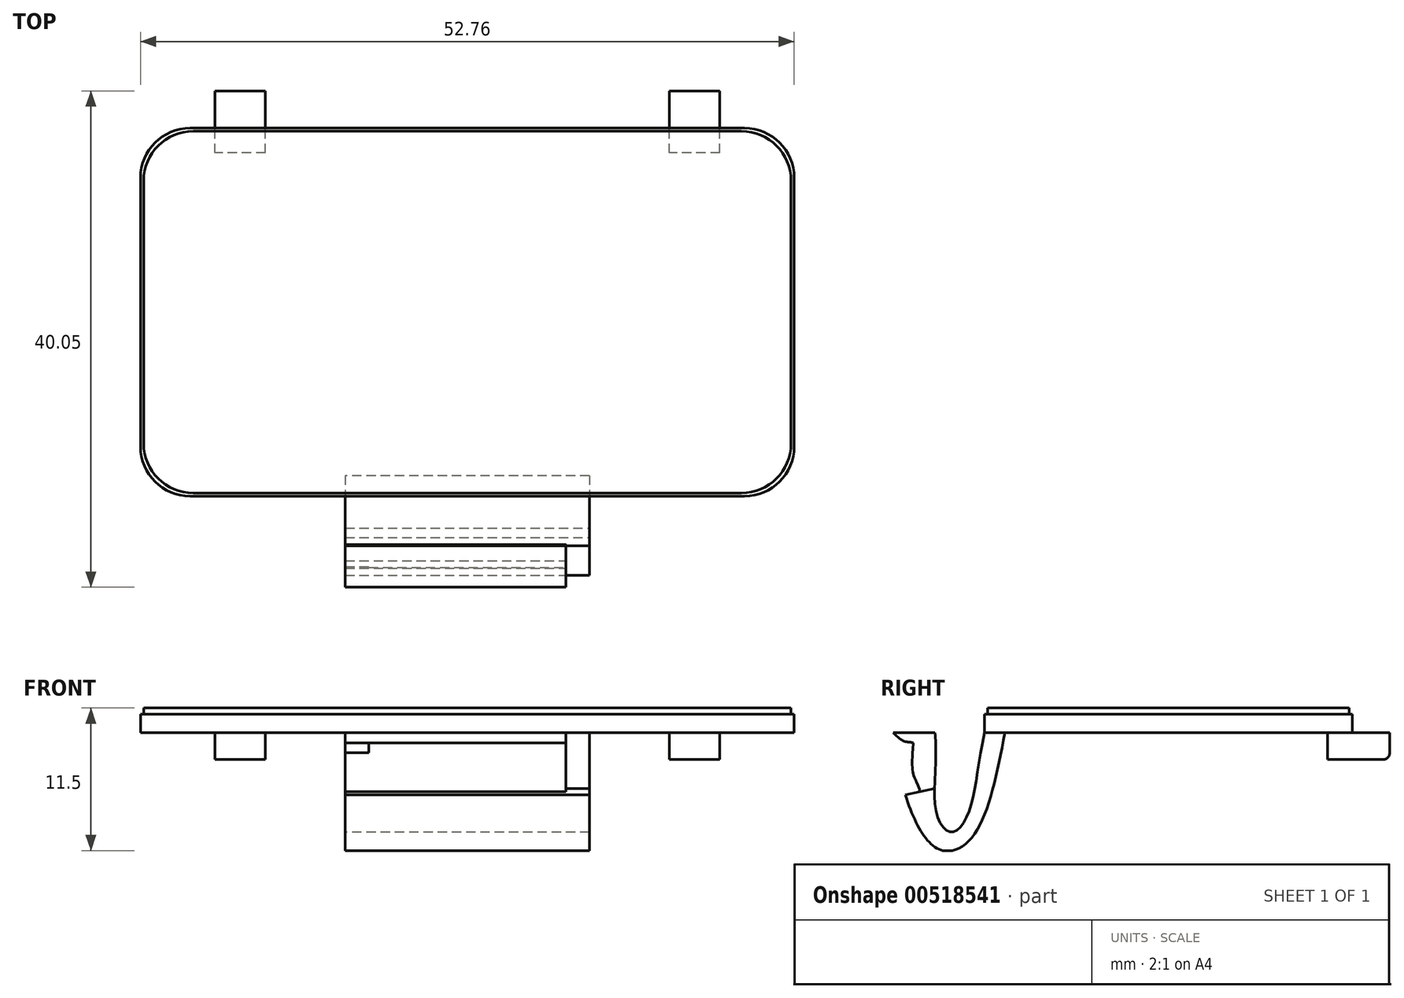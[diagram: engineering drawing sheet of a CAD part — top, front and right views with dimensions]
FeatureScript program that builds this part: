
annotation { "Feature Type Name" : "Feature", "Feature Type Description" : "" }
export const myFeature = defineFeature(function(context is Context, id is Id, definition is map)
    precondition{}
    {
        {
            var Q0;
            Q0=qCreatedBy(makeId("Top.planeOp"),FACE);
            var sketch = newSketch(context, id + "F0", { "sketchPlane" : qUnion([Q0])});
            skLineSegment(sketch, "E0.bottom", {"start": v(22.38, 14.85) * mm, "end": v(-22.38, 14.85) * mm});
            skLineSegment(sketch, "E0.top", {"start": v(22.38, -14.85) * mm, "end": v(-22.38, -14.85) * mm});
            skLineSegment(sketch, "E0.left", {"start": v(26.38, 10.85) * mm, "end": v(26.38, -10.85) * mm});
            skLineSegment(sketch, "E0.right", {"start": v(-26.38, 10.85) * mm, "end": v(-26.38, -10.85) * mm});
            skPoint(sketch, "E0.middle", {"position": v(0, 0) * mm});
            skPoint(sketch, "E1.visualSharp", {"position": v(26.38, 14.85) * mm});
            skArc(sketch, "E1.filletArc", {"start": v(26.38, 10.85) * mm, "mid": v(25.2, 13.68) * mm, "end": v(22.38, 14.85) * mm});
            skPoint(sketch, "E2.visualSharp", {"position": v(26.38, -14.85) * mm});
            skArc(sketch, "E2.filletArc", {"start": v(22.38, -14.85) * mm, "mid": v(25.2, -13.68) * mm, "end": v(26.38, -10.85) * mm});
            skPoint(sketch, "E3.visualSharp", {"position": v(-26.38, -14.85) * mm});
            skArc(sketch, "E3.filletArc", {"start": v(-26.38, -10.85) * mm, "mid": v(-25.2, -13.68) * mm, "end": v(-22.38, -14.85) * mm});
            skPoint(sketch, "E4.visualSharp", {"position": v(-26.38, 14.85) * mm});
            skArc(sketch, "E4.filletArc", {"start": v(-22.38, 14.85) * mm, "mid": v(-25.2, 13.68) * mm, "end": v(-26.38, 10.85) * mm});
            skSolve(sketch);
        }
        {
            var Q0;
            Q0=makeQuery(id+"F0.imprint","IMPRINT",FACE,{"disambiguationData":[TD([[makeQuery(id+"F0.imprint","IMPRINT",EDGE,{"derivedFrom":sQuery(id+"F0.wireOp",EDGE,"E0.bottom")}),1.0]])]});
            extrude(context, id + "F1", {"entities" : qUnion([Q0]), "depth" : 1.5 * mm, "offsetDistance" : 25.4 * mm});
        }
        {
            var Q0;
            Q0=makeQuery(id+"F1.opExtrude","CAP_FACE",FACE,{"disambiguationData":[OSD([sQuery(id+"F0.wireOp",EDGE,"E0.bottom"),sQuery(id+"F0.wireOp",EDGE,"E0.top"),sQuery(id+"F0.wireOp",EDGE,"E0.left"),sQuery(id+"F0.wireOp",EDGE,"E0.right"),sQuery(id+"F0.wireOp",EDGE,"E1.filletArc"),sQuery(id+"F0.wireOp",EDGE,"E2.filletArc"),sQuery(id+"F0.wireOp",EDGE,"E3.filletArc"),sQuery(id+"F0.wireOp",EDGE,"E4.filletArc")])],"isStart":false});
            var sketch = newSketch(context, id + "F2", { "sketchPlane" : qUnion([Q0])});
            skLineSegment(sketch, "E5.bottom", {"start": v(22.12, 14.6) * mm, "end": v(-22.13, 14.6) * mm});
            skLineSegment(sketch, "E5.top", {"start": v(22.12, -14.6) * mm, "end": v(-22.13, -14.6) * mm});
            skLineSegment(sketch, "E5.left", {"start": v(26.13, 10.6) * mm, "end": v(26.13, -10.6) * mm});
            skLineSegment(sketch, "E5.right", {"start": v(-26.13, 10.6) * mm, "end": v(-26.13, -10.6) * mm});
            skPoint(sketch, "E5.middle", {"position": v(0, 0) * mm});
            skPoint(sketch, "E6.visualSharp", {"position": v(-26.13, 14.6) * mm});
            skArc(sketch, "E6.filletArc", {"start": v(-22.13, 14.6) * mm, "mid": v(-24.95, 13.43) * mm, "end": v(-26.13, 10.6) * mm});
            skPoint(sketch, "E7.visualSharp", {"position": v(26.13, 14.6) * mm});
            skArc(sketch, "E7.filletArc", {"start": v(26.12, 10.6) * mm, "mid": v(24.95, 13.43) * mm, "end": v(22.12, 14.6) * mm});
            skPoint(sketch, "E8.visualSharp", {"position": v(26.13, -14.6) * mm});
            skArc(sketch, "E8.filletArc", {"start": v(22.12, -14.6) * mm, "mid": v(24.95, -13.43) * mm, "end": v(26.12, -10.6) * mm});
            skPoint(sketch, "E9.visualSharp", {"position": v(-26.13, -14.6) * mm});
            skArc(sketch, "E9.filletArc", {"start": v(-26.13, -10.6) * mm, "mid": v(-24.95, -13.43) * mm, "end": v(-22.13, -14.6) * mm});
            skSolve(sketch);
        }
        {
            var Q0;
            Q0=makeQuery(id+"F2.imprint","IMPRINT",FACE,{"disambiguationData":[TD([[makeQuery(id+"F2.imprint","IMPRINT",EDGE,{"derivedFrom":sQuery(id+"F2.wireOp",EDGE,"E5.bottom")}),1.0]])]});
            extrude(context, id + "F3", {"entities" : qUnion([Q0]), "operationType" : NewBodyOperationType.ADD, "depth" : 0.5 * mm, "offsetDistance" : 25.4 * mm});
        }
        {
            var Q0;
            Q0=makeQuery(id+"F0.imprint","IMPRINT",FACE,{"disambiguationData":[TD([[makeQuery(id+"F0.imprint","IMPRINT",EDGE,{"derivedFrom":sQuery(id+"F0.wireOp",EDGE,"E0.bottom")}),1.0]])]});
            var sketch = newSketch(context, id + "F4", { "sketchPlane" : qUnion([Q0])});
            skLineSegment(sketch, "E10.0", {"start": v(22.38, 14.85) * mm, "end": v(-22.38, 14.85) * mm, "construction": true});
            skLineSegment(sketch, "E10.1", {"start": v(22.38, -14.85) * mm, "end": v(-22.38, -14.85) * mm});
            skArc(sketch, "E10.2", {"start": v(22.38, -14.85) * mm, "mid": v(25.2, -13.68) * mm, "end": v(26.38, -10.85) * mm});
            skLineSegment(sketch, "E10.3", {"start": v(26.38, 10.85) * mm, "end": v(26.38, -10.85) * mm});
            skArc(sketch, "E10.4", {"start": v(26.38, 10.85) * mm, "mid": v(25.2, 13.68) * mm, "end": v(22.38, 14.85) * mm, "construction": true});
            skArc(sketch, "E10.5", {"start": v(-22.38, 14.85) * mm, "mid": v(-25.2, 13.68) * mm, "end": v(-26.38, 10.85) * mm, "construction": true});
            skLineSegment(sketch, "E10.6", {"start": v(-26.38, 10.85) * mm, "end": v(-26.38, -10.85) * mm});
            skArc(sketch, "E10.7", {"start": v(-26.38, -10.85) * mm, "mid": v(-25.2, -13.68) * mm, "end": v(-22.38, -14.85) * mm});
            skLineSegment(sketch, "E11", {"start": v(22.38, 14.85) * mm, "end": v(22.38, -14.85) * mm, "construction": true});
            skLineSegment(sketch, "E12", {"start": v(-22.38, 14.85) * mm, "end": v(-22.38, -14.85) * mm, "construction": true});
            skLineSegment(sketch, "E13.bottom", {"start": v(20.37, 12.85) * mm, "end": v(16.3, 12.85) * mm});
            skLineSegment(sketch, "E13.top", {"start": v(20.37, 17.85) * mm, "end": v(16.3, 17.85) * mm});
            skLineSegment(sketch, "E13.left", {"start": v(20.37, 12.85) * mm, "end": v(20.37, 17.85) * mm});
            skLineSegment(sketch, "E13.right", {"start": v(16.3, 12.85) * mm, "end": v(16.3, 17.85) * mm});
            skLineSegment(sketch, "E14.bottom", {"start": v(-16.3, 12.85) * mm, "end": v(-20.37, 12.85) * mm});
            skLineSegment(sketch, "E14.top", {"start": v(-16.3, 17.85) * mm, "end": v(-20.37, 17.85) * mm});
            skLineSegment(sketch, "E14.left", {"start": v(-16.3, 12.85) * mm, "end": v(-16.3, 17.85) * mm});
            skLineSegment(sketch, "E14.right", {"start": v(-20.37, 12.85) * mm, "end": v(-20.37, 17.85) * mm});
            skPoint(sketch, "E15", {"position": v(22.37, 12.85) * mm});
            skLineSegment(sketch, "E16", {"start": v(22.37, 12.85) * mm, "end": v(-25.84, 12.85) * mm, "construction": true});
            skLineSegment(sketch, "E17.bottom", {"start": v(9.86, -13.2) * mm, "end": v(-9.85, -13.2) * mm});
            skLineSegment(sketch, "E17.top", {"start": v(9.86, -23.2) * mm, "end": v(-9.85, -23.2) * mm});
            skLineSegment(sketch, "E17.left", {"start": v(9.86, -13.2) * mm, "end": v(9.86, -23.2) * mm});
            skLineSegment(sketch, "E17.right", {"start": v(-9.85, -13.2) * mm, "end": v(-9.85, -23.2) * mm});
            skLineSegment(sketch, "E18", {"start": v(22.38, -13.2) * mm, "end": v(-22.38, -13.2) * mm, "construction": true});
            skSolve(sketch);
        }
        {
            var Q0;
            {var subQ0=sQuery(id+"F4.wireOp",EDGE,"E14.top");Q0=makeQuery(id+"F4.imprint","IMPRINT",FACE,{"disambiguationData":[TD([[makeQuery(id+"F4.imprint","IMPRINT",EDGE,{"derivedFrom":subQ0}),1.0]])]});}
            var Q1;
            {var subQ0=sQuery(id+"F4.wireOp",EDGE,"E14.bottom");Q1=makeQuery(id+"F4.imprint","IMPRINT",FACE,{"disambiguationData":[TD([[makeQuery(id+"F4.imprint","IMPRINT",EDGE,{"derivedFrom":subQ0}),-1.0]])]});}
            var Q2;
            {var subQ0=sQuery(id+"F4.wireOp",EDGE,"E13.bottom");Q2=makeQuery(id+"F4.imprint","IMPRINT",FACE,{"disambiguationData":[TD([[makeQuery(id+"F4.imprint","IMPRINT",EDGE,{"derivedFrom":subQ0}),-1.0]])]});}
            var Q3;
            {var subQ0=sQuery(id+"F4.wireOp",EDGE,"E13.top");Q3=makeQuery(id+"F4.imprint","IMPRINT",FACE,{"disambiguationData":[TD([[makeQuery(id+"F4.imprint","IMPRINT",EDGE,{"derivedFrom":subQ0}),1.0]])]});}
            extrude(context, id + "F5", {"entities" : qUnion([Q0, Q1, Q2, Q3]), "operationType" : NewBodyOperationType.ADD, "oppositeDirection" : true, "depth" : 2.15 * mm, "offsetDistance" : 25.4 * mm});
        }
        {
            var Q0;
            {var subQ5=sQuery(id+"F4.wireOp",EDGE,"E17.top");Q0=makeQuery(id+"F4.imprint","IMPRINT",FACE,{"disambiguationData":[TD([[makeQuery(id+"F4.imprint","IMPRINT",EDGE,{"derivedFrom":subQ5}),-1.0]])]});}
            var Q1;
            {var subQ5=sQuery(id+"F4.wireOp",EDGE,"E17.bottom");Q1=makeQuery(id+"F4.imprint","IMPRINT",FACE,{"disambiguationData":[TD([[makeQuery(id+"F4.imprint","IMPRINT",EDGE,{"derivedFrom":subQ5}),1.0]])]});}
            extrude(context, id + "F6", {"entities" : qUnion([Q0, Q1]), "operationType" : NewBodyOperationType.ADD, "oppositeDirection" : true, "depth" : 9.5 * mm, "offsetDistance" : 25.4 * mm});
        }
        {
            var Q0;
            Q0=makeQuery(id+"F6.opExtrude","SWEPT_FACE",FACE,{"disambiguationData":[OSD([sQuery(id+"F4.wireOp",EDGE,"E17.left")])]});
            var sketch = newSketch(context, id + "F7", { "sketchPlane" : qUnion([Q0])});
            skFitSpline(sketch, "E19", {"points": [v(-13.2, 0) * mm, v(-15.8, -8.37) * mm, v(-18.2, -9.5) * mm, v(-20.35, -7.25) * mm, v(-22.2, 0) * mm], "startDerivative": vector(-5.73, -30.33) * mm, "endDerivative": vector(-2.29, 26.07) * mm});
            skFitSpline(sketch, "E20", {"points": [v(-14.85, 0) * mm, v(-16.2, -6.6) * mm, v(-17.54, -8.02) * mm, v(-18.74, -6.36) * mm, v(-18.85, 0) * mm], "startDerivative": vector(-5.19, -24.46) * mm, "endDerivative": vector(-2.61, 22.44) * mm});
            skPoint(sketch, "E21", {"position": v(-17.54, -9.52) * mm});
            skFitSpline(sketch, "E22", {"points": [v(-22.2, 0) * mm, v(-21.35, -0.67) * mm, v(-20.6, -0.8) * mm], "startDerivative": vector(0.98, -1.06) * mm, "endDerivative": vector(1.84, -0.57) * mm});
            skPoint(sketch, "E23", {"position": v(-18.87, -4.5) * mm});
            skPoint(sketch, "E24", {"position": v(-21.23, -5) * mm});
            skLineSegment(sketch, "E25", {"start": v(-18.87, -4.5) * mm, "end": v(-21.23, -5) * mm});
            skFitSpline(sketch, "E26", {"points": [v(-20.6, -0.8) * mm, v(-20.6, -3.29) * mm, v(-20.05, -4.75) * mm], "startDerivative": vector(-0.17, -3.92) * mm, "endDerivative": vector(0.9, -4.59) * mm});
            skSolve(sketch);
        }
        {
            var Q0;
            {var subQ0=sQuery(id+"F4.wireOp",EDGE,"E17.left");var subQ2=sQuery(id+"F4.wireOp",EDGE,"E17.top");var subQ3=makeQuery(id+"F6.opExtrude","SWEPT_EDGE",EDGE,{"disambiguationData":[OSD([subQ2,subQ0])]});Q0=makeQuery(id+"F7.imprint","IMPRINT",FACE,{"disambiguationData":[TD([[makeQuery(id+"F7.imprint","IMPRINT",EDGE,{"derivedFrom":subQ3}),-1.0]])]});}
            extrude(context, id + "F8", {"entities" : qUnion([Q0]), "operationType" : NewBodyOperationType.REMOVE, "oppositeDirection" : true, "depth" : 25.4 * mm, "offsetDistance" : 25.4 * mm});
        }
        {
            var Q0;
            {var subQ0=sQuery(id+"F7.wireOp",EDGE,"E20");var subQ6=makeQuery(id+"F7.imprint","INTERSECT",VERTEX,{"derivedFrom":[subQ0,sQuery(id+"F7.wireOp",EDGE,"E25")]});Q0=makeQuery(id+"F7.imprint","IMPRINT",FACE,{"disambiguationData":[TD([[makeQuery(id+"F7.imprint","IMPRINT",EDGE,{"disambiguationData":[TD([[subQ6,-1.0]])],"derivedFrom":subQ0}),-1.0]])]});}
            extrude(context, id + "F9", {"entities" : qUnion([Q0]), "operationType" : NewBodyOperationType.REMOVE, "oppositeDirection" : true, "depth" : 25.4 * mm, "offsetDistance" : 25.4 * mm});
        }
        {
            var Q0;
            {var subQ1=sQuery(id+"F4.wireOp",EDGE,"E17.left");var subQ2=makeQuery(id+"F6.opExtrude","SWEPT_EDGE",EDGE,{"disambiguationData":[OSD([sQuery(id+"F4.wireOp",EDGE,"E17.bottom"),subQ1])]});Q0=makeQuery(id+"F7.imprint","IMPRINT",FACE,{"disambiguationData":[TD([[makeQuery(id+"F7.imprint","IMPRINT",EDGE,{"derivedFrom":subQ2}),1.0]])]});}
            extrude(context, id + "F10", {"entities" : qUnion([Q0]), "operationType" : NewBodyOperationType.REMOVE, "oppositeDirection" : true, "depth" : 25.4 * mm, "offsetDistance" : 25.4 * mm});
        }
        {
            var Q0;
            {var subQ0=sQuery(id+"F7.wireOp",EDGE,"E22");Q0=makeQuery(id+"F7.imprint","IMPRINT",FACE,{"disambiguationData":[TD([[makeQuery(id+"F7.imprint","IMPRINT",EDGE,{"derivedFrom":subQ0}),-1.0]])]});}
            extrude(context, id + "F11", {"entities" : qUnion([Q0]), "operationType" : NewBodyOperationType.REMOVE, "oppositeDirection" : true, "depth" : 25.4 * mm, "offsetDistance" : 25.4 * mm});
        }
        {
            var Q0;
            {var subQ4=sQuery(id+"F7.wireOp",EDGE,"E22");Q0=makeQuery(id+"F7.imprint","IMPRINT",FACE,{"disambiguationData":[TD([[makeQuery(id+"F7.imprint","IMPRINT",EDGE,{"derivedFrom":subQ4}),1.0]])]});}
            extrude(context, id + "F12", {"entities" : qUnion([Q0]), "operationType" : NewBodyOperationType.REMOVE, "oppositeDirection" : true, "depth" : 1.9 * mm, "offsetDistance" : 25.4 * mm});
        }
        {
            var Q0;
            Q0=makeQuery(id+"F6.opExtrude","SWEPT_FACE",FACE,{"disambiguationData":[OSD([sQuery(id+"F4.wireOp",EDGE,"E17.right")])]});
            var sketch = newSketch(context, id + "F13", { "sketchPlane" : qUnion([Q0])});
            skLineSegment(sketch, "E27.0", {"start": v(18.87, -4.5) * mm, "end": v(21.23, -5) * mm});
            skFitSpline(sketch, "E27.1", {"points": [v(20.6, -0.8) * mm, v(20.63, -1.53) * mm, v(20.86, -3.5) * mm, v(20.17, -4.07) * mm, v(20.04, -4.75) * mm]});
            skFitSpline(sketch, "E27.2", {"points": [v(14.85, 0) * mm, v(15.4, -2.58) * mm, v(15.42, -6.3) * mm, v(17.6, -9.42) * mm, v(19.33, -5.94) * mm, v(18.58, -2.3) * mm, v(18.85, 0) * mm]});
            skLineSegment(sketch, "E27.3", {"start": v(18.85, 0) * mm, "end": v(22.2, 0) * mm});
            skFitSpline(sketch, "E27.4", {"points": [v(22.2, 0) * mm, v(22.02, -0.2) * mm, v(21.34, -0.84) * mm, v(20.88, -0.72) * mm, v(20.6, -0.8) * mm]});
            skSolve(sketch);
        }
        {
            var Q0;
            {var subQ4=sQuery(id+"F13.wireOp",EDGE,"E27.1");Q0=makeQuery(id+"F13.imprint","IMPRINT",FACE,{"disambiguationData":[TD([[makeQuery(id+"F13.imprint","IMPRINT",EDGE,{"derivedFrom":subQ4}),1.0]])]});}
            extrude(context, id + "F14", {"entities" : qUnion([Q0]), "operationType" : NewBodyOperationType.REMOVE, "oppositeDirection" : true, "depth" : 1.9 * mm, "offsetDistance" : 25.4 * mm});
        }
        {
            var Q0;
            Q0=makeQuery(id+"F5.opExtrude","CAP_EDGE",EDGE,{"disambiguationData":[OSD([sQuery(id+"F4.wireOp",EDGE,"E13.top")])],"isStart":false});
            var Q1;
            Q1=makeQuery(id+"F5.opExtrude","CAP_EDGE",EDGE,{"disambiguationData":[OSD([sQuery(id+"F4.wireOp",EDGE,"E14.top")])],"isStart":false});
            fillet(context, id + "F15", {"entities" : qUnion([Q0, Q1]), "radius" : .5 * mm, "tangentPropagation" : true, "allowEdgeOverflow" : false});
        }
    });
